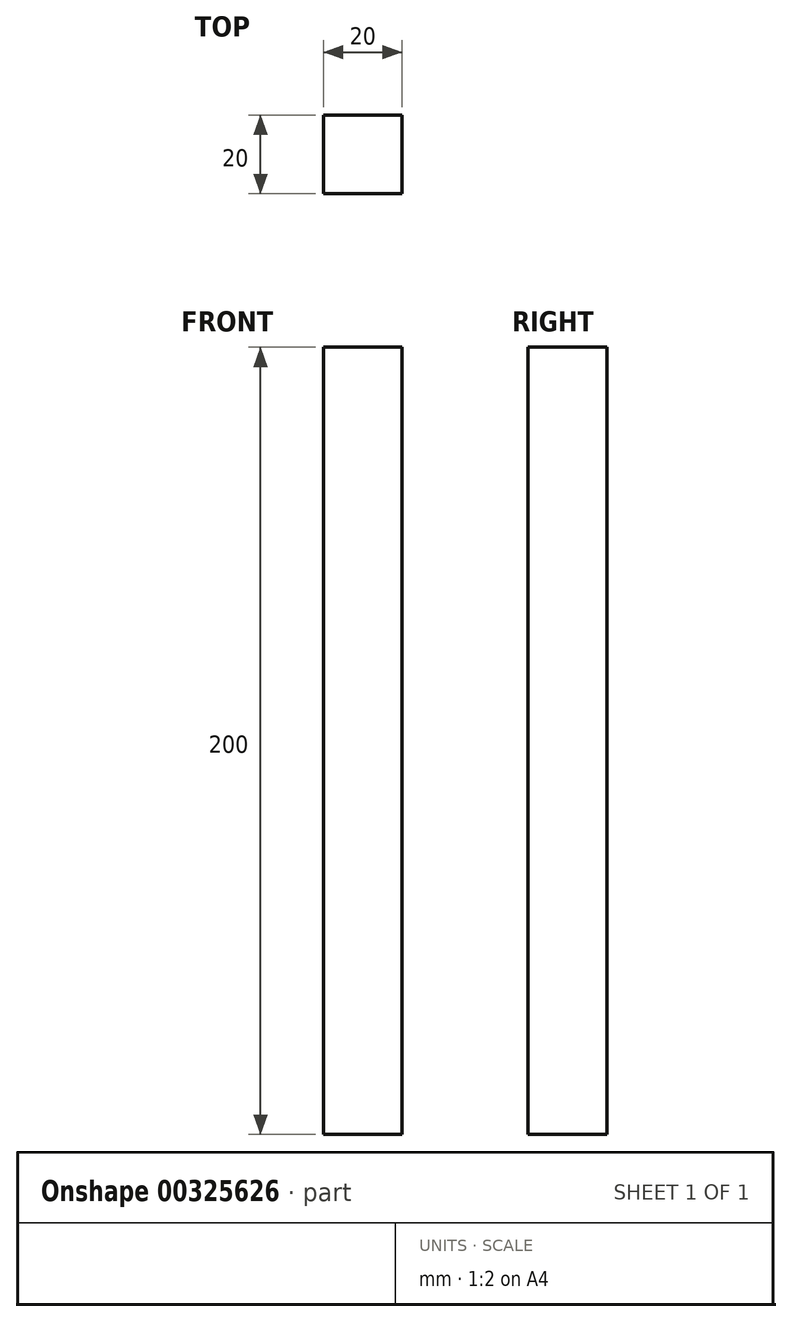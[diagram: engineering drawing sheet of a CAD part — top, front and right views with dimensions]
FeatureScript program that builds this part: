
annotation { "Feature Type Name" : "Feature", "Feature Type Description" : "" }
export const myFeature = defineFeature(function(context is Context, id is Id, definition is map)
    precondition{}
    {
        {
            var Q0;
            Q0=qCreatedBy(makeId("Top.planeOp"),FACE);
            var sketch = newSketch(context, id + "F0", { "sketchPlane" : qUnion([Q0])});
            skLineSegment(sketch, "E0.bottom", {"start": v(0, 0) * mm, "end": v(20, 0) * mm});
            skLineSegment(sketch, "E0.top", {"start": v(0, 20) * mm, "end": v(20, 20) * mm});
            skLineSegment(sketch, "E0.left", {"start": v(0, 0) * mm, "end": v(0, 20) * mm});
            skLineSegment(sketch, "E0.right", {"start": v(20, 0) * mm, "end": v(20, 20) * mm});
            skSolve(sketch);
        }
        {
            var Q0;
            Q0=makeQuery(id+"F0.imprint","IMPRINT",FACE,{"disambiguationData":[TD([[makeQuery(id+"F0.imprint","IMPRINT",EDGE,{"derivedFrom":sQuery(id+"F0.wireOp",EDGE,"E0.bottom")}),1.0]])]});
            extrude(context, id + "F1", {"entities" : qUnion([Q0]), "depth" : 200 * mm});
        }
    });
